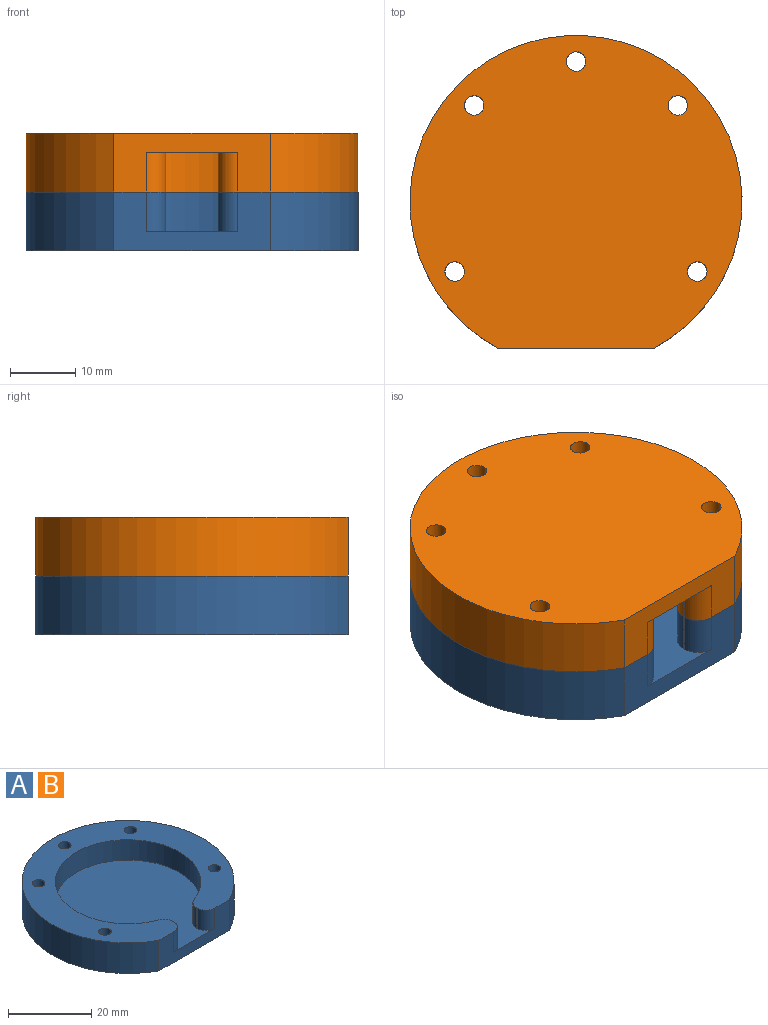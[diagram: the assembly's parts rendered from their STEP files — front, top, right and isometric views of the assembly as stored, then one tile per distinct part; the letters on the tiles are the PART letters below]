
ASSEMBLY  parts=2 mates=1
PART A: 17 faces, bbox 51x48x9 mm
  f0: plane 6x0.23mm, normal (1,0,0), area 1.4mm2, adj f5,f7,f11,f14
  f1: cylinder r=17.5mm len=35mm, axis (0,0,-1), area 586.6mm2, adj f5,f7,f11,f12
  f2: plane 6x0.23mm, normal (-1,0,0), area 1.4mm2, adj f5,f7,f12,f13
  f3: cylinder r=25.5mm len=51mm, axis (0,0,-1), area 1217.1mm2, adj f4,f5,f6
  f4: plane 24x9mm, normal (0,-1,0), area 132mm2, adj f3,f5,f6,f7,f13,f14
  f5: plane 51x48mm, normal (0,0,1), area 949.9mm2, adj f0,f1,f2,f3,f4,f8,f9,f10
  f6: plane 51x48mm, normal (0,0,-1), area 1958.9mm2, adj f3,f4,f8,f9,f10,f15,f16
  f7: plane 40x35mm, normal (0,0,1), area 1009mm2, adj f0,f1,f2,f4,f11,f12,f13,f14
  f8: cylinder r=1.5mm len=9mm, axis (0,0,-1), area 84.8mm2, adj f5,f6
  f9: cylinder r=1.5mm len=9mm, axis (0,0,-1), area 84.8mm2, adj f5,f6
  f10: cylinder r=1.5mm len=9mm, axis (0,0,-1), area 84.8mm2, adj f5,f6
  f11: cylinder r=3mm len=6mm, axis (0,0,-1), area 22mm2, adj f0,f1,f5,f7
  f12: cylinder r=3mm len=6mm, axis (0,0,-1), area 22mm2, adj f1,f2,f5,f7
  f13: cylinder r=3mm len=6mm, axis (0,0,1), area 28.3mm2, adj f2,f4,f5,f7
  f14: cylinder r=3mm len=6mm, axis (0,0,1), area 28.3mm2, adj f0,f4,f5,f7
  f15: cylinder r=1.5mm len=9mm, axis (0,0,-1), area 84.8mm2, adj f5,f6
  f16: cylinder r=1.5mm len=9mm, axis (0,0,-1), area 84.8mm2, adj f5,f6
PART B: same geometry as A
PLACE A t=(-16.58,-9.33,7.15)mm fixed
PLACE B rot(axis=(0,-1,0),180deg) t=(-16.58,-9.33,25.15)mm
MATE revolute B.f10 <-> A.f8  axis (0,0,1) through (2.04,-20.08,16.15)mm
